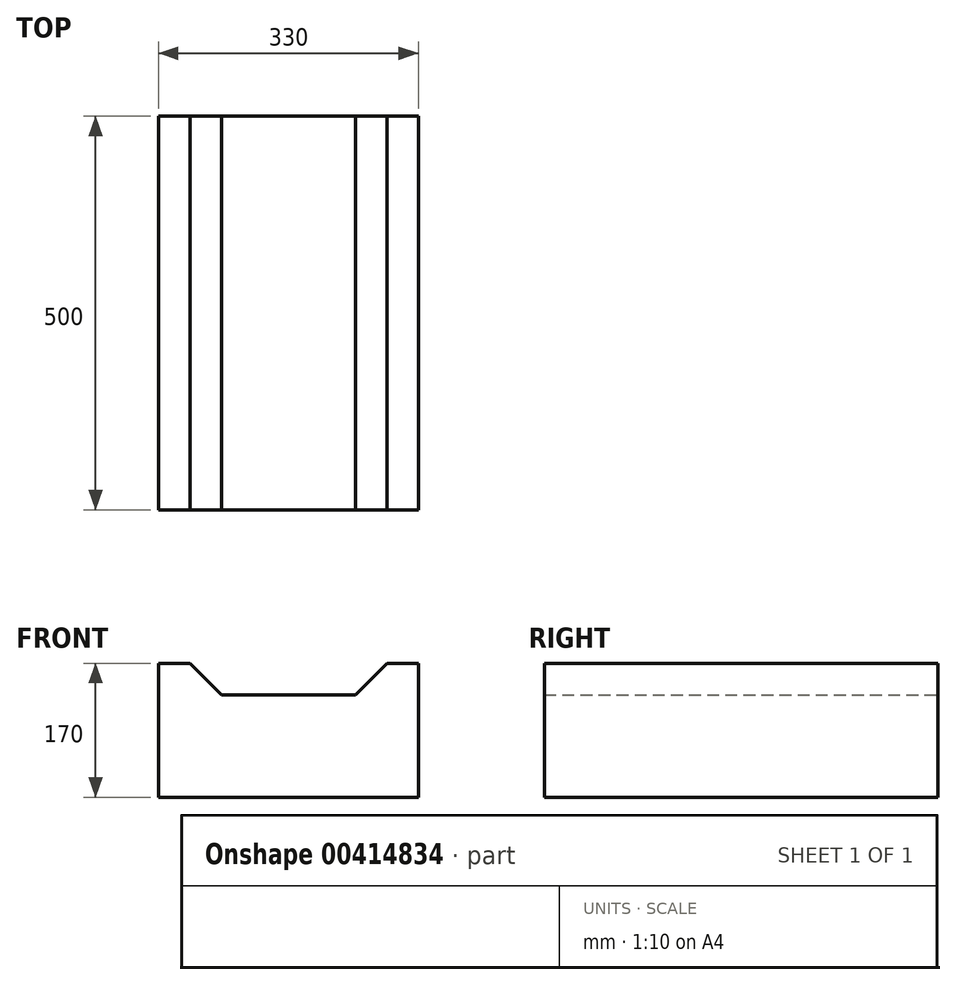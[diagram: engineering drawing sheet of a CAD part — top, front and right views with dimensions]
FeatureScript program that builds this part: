
annotation { "Feature Type Name" : "Feature", "Feature Type Description" : "" }
export const myFeature = defineFeature(function(context is Context, id is Id, definition is map)
    precondition{}
    {
        {
            var Q0;
            Q0=qCreatedBy(makeId("Front.planeOp"),FACE);
            var sketch = newSketch(context, id + "F0", { "sketchPlane" : qUnion([Q0])});
            skLineSegment(sketch, "E0", {"start": v(0, 0) * mm, "end": v(330, 0) * mm});
            skLineSegment(sketch, "E1", {"start": v(330, 0) * mm, "end": v(330, 170) * mm});
            skLineSegment(sketch, "E2", {"start": v(330, 170) * mm, "end": v(290, 170) * mm});
            skLineSegment(sketch, "E3", {"start": v(0, 170) * mm, "end": v(0, 0) * mm});
            skLineSegment(sketch, "E4", {"start": v(80, 130) * mm, "end": v(250, 130) * mm});
            skLineSegment(sketch, "E5", {"start": v(250, 130) * mm, "end": v(290, 170) * mm});
            skLineSegment(sketch, "E6", {"start": v(80, 130) * mm, "end": v(40, 170) * mm});
            skLineSegment(sketch, "E7.trimOffspring", {"start": v(40, 170) * mm, "end": v(0, 170) * mm});
            skSolve(sketch);
        }
        {
            var Q0;
            Q0 = qSketchRegion(id + "F0", true);
            extrude(context, id + "F1", {"entities" : qUnion([Q0]), "depth" : 500 * mm});
        }
    });
